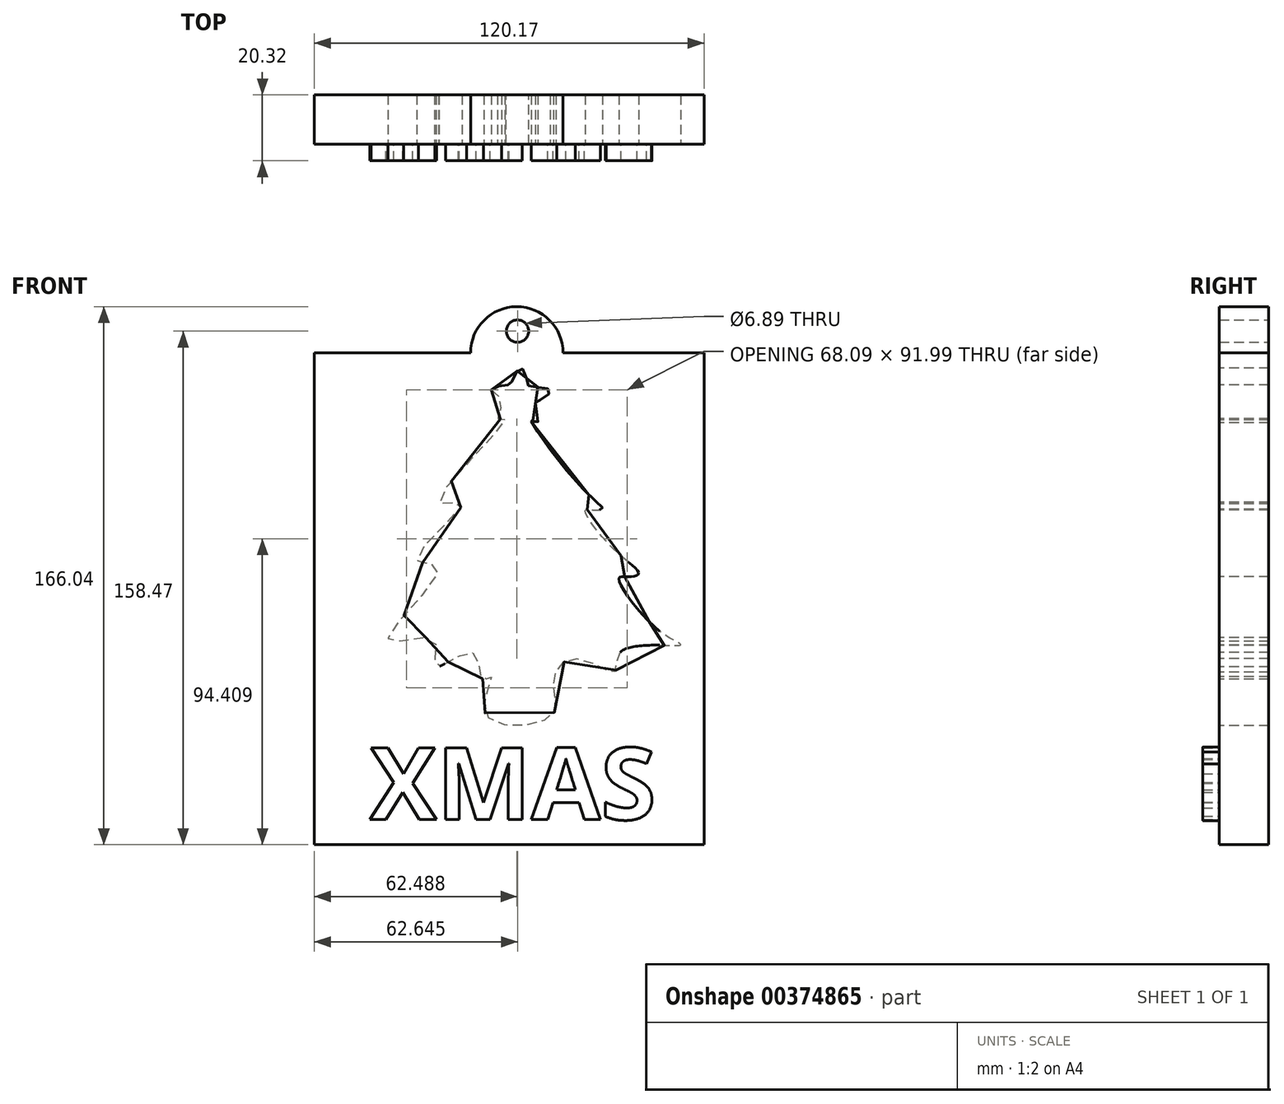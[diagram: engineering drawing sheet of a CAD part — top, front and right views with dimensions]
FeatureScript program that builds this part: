
annotation { "Feature Type Name" : "Feature", "Feature Type Description" : "" }
export const myFeature = defineFeature(function(context is Context, id is Id, definition is map)
    precondition{}
    {
        {
            var Q0;
            Q0=qCreatedBy(makeId("Front.planeOp"),FACE);
            var sketch = newSketch(context, id + "F0", { "sketchPlane" : qUnion([Q0])});
            skLineSegment(sketch, "E0.bottom", {"start": v(-57.68, 75.13) * mm, "end": v(62.5, 75.13) * mm});
            skLineSegment(sketch, "E0.top", {"start": v(-57.68, -76.65) * mm, "end": v(62.5, -76.65) * mm});
            skLineSegment(sketch, "E0.left", {"start": v(-57.68, 75.13) * mm, "end": v(-57.68, -76.65) * mm});
            skLineSegment(sketch, "E0.right", {"start": v(62.5, 75.13) * mm, "end": v(62.5, -76.65) * mm});
            skFitSpline(sketch, "E1", {"points": [v(-3.08, 63.76) * mm, v(0, 60.4) * mm, v(-1, 54.8) * mm, v(1.1, 54.52) * mm, v(-19.21, 29.09) * mm, v(-12.14, 28.67) * mm, v(-26.12, 11.45) * mm, v(-19.42, 8.6) * mm, v(-34.98, -13.31) * mm, v(-20.93, -13.48) * mm, v(-20.26, -21.68) * mm, v(-8.88, -17.5) * mm, v(-5.7, -25.53) * mm, v(-3.12, -24.81) * mm, v(-4.8, -36.49) * mm, v(15.6, -36.77) * mm, v(16.02, -26.5) * mm, v(22.91, -19.18) * mm, v(35.01, -23.26) * mm, v(36.7, -17.21) * mm, v(55.13, -15.1) * mm, v(49.36, -11.17) * mm, v(36.28, 5.58) * mm, v(38.95, 6) * mm, v(42.33, 6.97) * mm, v(36.02, 13.23) * mm, v(25.89, 26.45) * mm, v(28.18, 26.67) * mm, v(31.14, 26.95) * mm, v(25.09, 33.14) * mm, v(9.22, 54.34) * mm, v(10.46, 53.74) * mm, v(11.23, 53.74) * mm, v(10.46, 59.6) * mm, v(11.35, 60.31) * mm, v(15.07, 63.5) * mm, v(8.7, 64.82) * mm, v(8.19, 65.66) * mm, v(5.93, 70.43) * mm, v(2.67, 65.4) * mm, v(1.66, 65.24) * mm, v(-3.08, 63.76) * mm]});
            skArc(sketch, "E2", {"start": v(19.03, 75.13) * mm, "mid": v(4.76, 89.4) * mm, "end": v(-9.5, 75.13) * mm});
            skCircle(sketch, "E3", {"center": v(4.97, 81.82) * mm, "radius": 3.45 * mm});
            skSolve(sketch);
        }
        {
            var Q0;
            Q0 = qSketchRegion(id + "F0", true);
            extrude(context, id + "F1", {"entities" : qUnion([Q0]), "depth" : 12.7 * mm});
        }
        {
            var Q0;
            Q0=makeQuery(id+"F1.opExtrude","CAP_FACE",FACE,{"disambiguationData":[OSD([sQuery(id+"F0.wireOp",EDGE,"E0.bottom"),sQuery(id+"F0.wireOp",EDGE,"E0.top"),sQuery(id+"F0.wireOp",EDGE,"E0.left"),sQuery(id+"F0.wireOp",EDGE,"E0.right"),sQuery(id+"F0.wireOp",EDGE,"E1")])],"isStart":false});
            extrude(context, id + "F2", {"entities" : qUnion([Q0]), "operationType" : NewBodyOperationType.ADD, "depth" : 2.54 * mm});
        }
        {
            var Q0;
            Q0=makeQuery(id+"F2.opExtrude","CAP_FACE",FACE,{"disambiguationData":[OSD([sQuery(id+"F0.wireOp",EDGE,"E0.bottom"),sQuery(id+"F0.wireOp",EDGE,"E0.top"),sQuery(id+"F0.wireOp",EDGE,"E0.left"),sQuery(id+"F0.wireOp",EDGE,"E0.right"),sQuery(id+"F0.wireOp",EDGE,"E1"),sQuery(id+"F0.wireOp",EDGE,"E2"),sQuery(id+"F0.wireOp",EDGE,"E3")])],"isStart":false});
            var sketch = newSketch(context, id + "F3", { "sketchPlane" : qUnion([Q0])});
            skText(sketch, "E4", { "text": "XMAS", "fontName": "OpenSans-Bold.ttf"});
            const initialGuessF3  = {"E4": [-0.0406, -0.0689, 1, 0, 0.02229]};
            skSetInitialGuess(sketch, initialGuessF3);
            skSolve(sketch);
        }
        {
            var Q0;
            Q0 = qSketchRegion(id + "F3", true);
            extrude(context, id + "F4", {"entities" : qUnion([Q0]), "operationType" : NewBodyOperationType.ADD, "depth" : 5.08 * mm});
        }
    });
